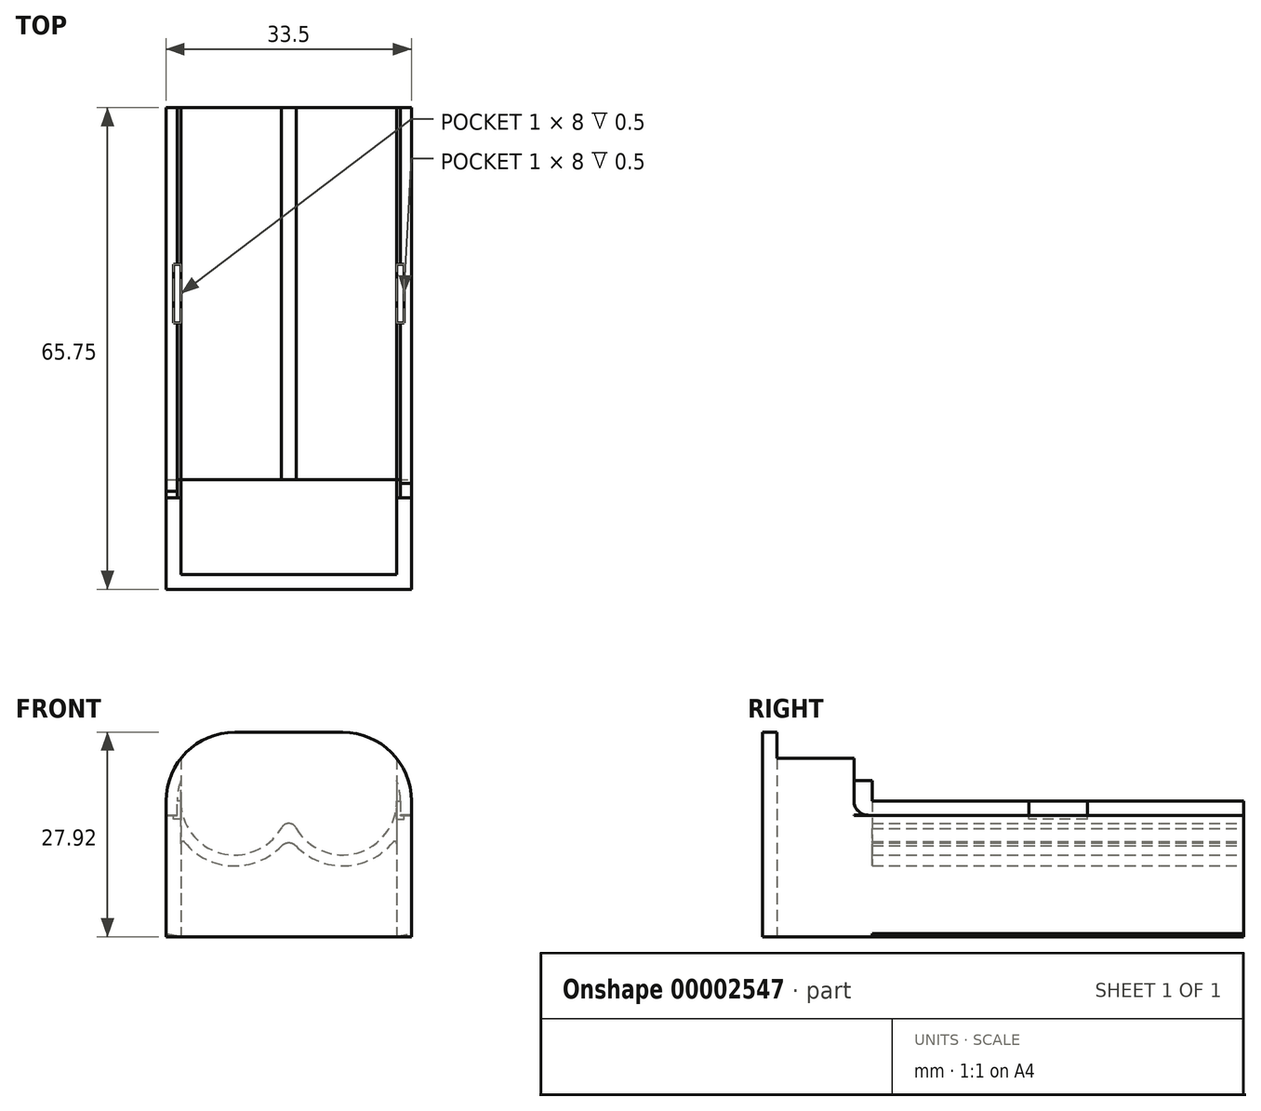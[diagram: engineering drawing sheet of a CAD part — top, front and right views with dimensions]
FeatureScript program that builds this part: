
annotation { "Feature Type Name" : "Feature", "Feature Type Description" : "" }
export const myFeature = defineFeature(function(context is Context, id is Id, definition is map)
    precondition{}
    {
        {
            var Q0;
            Q0=qCreatedBy(makeId("Front.planeOp"),FACE);
            var sketch = newSketch(context, id + "F0", { "sketchPlane" : qUnion([Q0])});
            skPoint(sketch, "E0.left.start.orphan", {"position": v(-29.5, 4.5) * mm});
            skArc(sketch, "E1", {"start": v(-29.31, 7.36) * mm, "mid": v(-23.14, 1.7) * mm, "end": v(-15.66, 5.45) * mm});
            skLineSegment(sketch, "E2.trimOffspring", {"start": v(-14.75, 9) * mm, "end": v(-14.75, 9) * mm});
            skPoint(sketch, "E3.end.orphan", {"position": v(-29.5, 9) * mm});
            skArc(sketch, "E4", {"start": v(-28.97, 3.35) * mm, "mid": v(-22.45, 0.13) * mm, "end": v(-15.71, 2.86) * mm});
            skPoint(sketch, "E5.top.start.orphan", {"position": v(-29.5, 0) * mm});
            skArc(sketch, "E6", {"start": v(-14.75, 3.25) * mm, "mid": v(-15.27, 3.15) * mm, "end": v(-15.71, 2.86) * mm});
            skLineSegment(sketch, "E7", {"start": v(-29.5, 9) * mm, "end": v(-30, 9) * mm});
            skLineSegment(sketch, "E8", {"start": v(-30, 9) * mm, "end": v(-30, 7.06) * mm});
            skLineSegment(sketch, "E9", {"start": v(-30.06, 7) * mm, "end": v(-31.5, 7) * mm});
            skLineSegment(sketch, "E10", {"start": v(-31.5, 7) * mm, "end": v(-31.5, -9.1) * mm});
            skLineSegment(sketch, "E11", {"start": v(-29.5, 3.16) * mm, "end": v(-29.5, -9.54) * mm});
            skArc(sketch, "E12", {"start": v(-28.97, 3.35) * mm, "mid": v(-29.3, 3.44) * mm, "end": v(-29.5, 3.16) * mm});
            skArc(sketch, "E13.trimOffspring", {"start": v(-14.75, 5.91) * mm, "mid": v(-15.37, 5.73) * mm, "end": v(-15.78, 5.24) * mm});
            skPoint(sketch, "E14.end.orphan", {"position": v(-0.19, 7.36) * mm});
            skPoint(sketch, "E14.start.orphan", {"position": v(0, 7.36) * mm});
            skPoint(sketch, "E15.center.orphan", {"position": v(-7.38, 9) * mm});
            skPoint(sketch, "E16.1.MirrorP", {"position": v(0, 0) * mm});
            skPoint(sketch, "E16.6.MirrorP", {"position": v(0, 4.5) * mm});
            skPoint(sketch, "E16.14.MirrorP", {"position": v(0, 9) * mm});
            skPoint(sketch, "E17.orphan", {"position": v(-29.31, 9) * mm});
            skArc(sketch, "E18", {"start": v(-29.5, 9) * mm, "mid": v(-29.45, 8.17) * mm, "end": v(-29.31, 7.36) * mm});
            skPoint(sketch, "E19.visualSharp", {"position": v(-30, 7) * mm});
            skArc(sketch, "E19.filletArc", {"start": v(-30.06, 7) * mm, "mid": v(-30.02, 7.02) * mm, "end": v(-30, 7.06) * mm});
            skLineSegment(sketch, "E20", {"start": v(-14.75, 5.91) * mm, "end": v(-14.75, 3.25) * mm});
            skArc(sketch, "E21.0.MirrorCS", {"start": v(0.56, 7) * mm, "mid": v(0.52, 7.02) * mm, "end": v(0.5, 7.06) * mm});
            skPoint(sketch, "E21.1.MirrorP", {"position": v(-0.19, 9) * mm});
            skLineSegment(sketch, "E21.2.MirrorCS", {"start": v(0, 9) * mm, "end": v(0.5, 9) * mm});
            skPoint(sketch, "E21.4.MirrorP", {"position": v(0.5, 7) * mm});
            skLineSegment(sketch, "E21.5.MirrorCS", {"start": v(0.56, 7) * mm, "end": v(2, 7) * mm});
            skLineSegment(sketch, "E21.7.MirrorCS", {"start": v(0.5, 9) * mm, "end": v(0.5, 7.06) * mm});
            skArc(sketch, "E21.9.MirrorCS", {"start": v(0, 9) * mm, "mid": v(-0.05, 8.17) * mm, "end": v(-0.19, 7.36) * mm});
            skArc(sketch, "E21.10.MirrorCS", {"start": v(-0.19, 7.36) * mm, "mid": v(-6.36, 1.7) * mm, "end": v(-13.84, 5.45) * mm});
            skArc(sketch, "E21.11.MirrorCS", {"start": v(-14.75, 3.25) * mm, "mid": v(-14.23, 3.15) * mm, "end": v(-13.79, 2.86) * mm});
            skArc(sketch, "E21.12.MirrorCS", {"start": v(-0.53, 3.35) * mm, "mid": v(-7.05, 0.13) * mm, "end": v(-13.79, 2.86) * mm});
            skLineSegment(sketch, "E21.13.MirrorCS", {"start": v(0, 3.16) * mm, "end": v(0, -9.54) * mm});
            skArc(sketch, "E21.15.MirrorCS", {"start": v(-14.75, 5.91) * mm, "mid": v(-14.13, 5.73) * mm, "end": v(-13.72, 5.24) * mm});
            skArc(sketch, "E21.16.MirrorCS", {"start": v(-0.53, 3.35) * mm, "mid": v(-0.2, 3.44) * mm, "end": v(0, 3.16) * mm});
            skLineSegment(sketch, "E21.19.MirrorCS", {"start": v(2, 7) * mm, "end": v(2, -9.1) * mm});
            skArc(sketch, "E22", {"start": v(-31.5, -9.1) * mm, "mid": v(-30.5, -9.33) * mm, "end": v(-29.5, -9.54) * mm});
            skArc(sketch, "E23.trimOffspring", {"start": v(0, -9.54) * mm, "mid": v(1, -9.33) * mm, "end": v(2, -9.1) * mm});
            skPoint(sketch, "E24.orphan", {"position": v(2, -6.36) * mm});
            skPoint(sketch, "E25.orphan", {"position": v(0, -6.36) * mm});
            skPoint(sketch, "E26.end.orphan", {"position": v(-29.5, -6.36) * mm});
            skPoint(sketch, "E27.orphan", {"position": v(-31.5, -6.36) * mm});
            skSolve(sketch);
        }
        {
            var Q0;
            Q0 = qSketchRegion(id + "F0", true);
            extrude(context, id + "F1", {"entities" : qUnion([Q0]), "depth" : 50.75 * mm});
        }
        {
            var Q0;
            Q0=makeQuery(id+"F1.opExtrude","SWEPT_FACE",FACE,{"disambiguationData":[OSD([sQuery(id+"F0.wireOp",EDGE,"E7")])]});
            var sketch = newSketch(context, id + "F2", { "sketchPlane" : qUnion([Q0])});
            skLineSegment(sketch, "E28.bottom", {"start": v(-29.5, -21.38) * mm, "end": v(-30.5, -21.38) * mm});
            skLineSegment(sketch, "E28.top", {"start": v(-29.5, -29.38) * mm, "end": v(-30.5, -29.38) * mm});
            skLineSegment(sketch, "E28.left", {"start": v(-29.5, -21.38) * mm, "end": v(-29.5, -29.38) * mm});
            skLineSegment(sketch, "E28.right", {"start": v(-30.5, -21.38) * mm, "end": v(-30.5, -29.38) * mm});
            skPoint(sketch, "E29", {"position": v(-29.5, -25.38) * mm});
            skSolve(sketch);
        }
        {
            var Q0;
            {var subQ7=sQuery(id+"F2.wireOp",EDGE,"E28.right");var subQ8=sQuery(id+"F2.wireOp",EDGE,"E28.left");Q0=qUnion([makeQuery(id+"F2.imprint","IMPRINT",FACE,{"disambiguationData":[TD([[makeQuery(id+"F2.imprint","IMPRINT",EDGE,{"derivedFrom":subQ7}),1.0]])]}),makeQuery(id+"F2.imprint","IMPRINT",FACE,{"disambiguationData":[TD([[makeQuery(id+"F2.imprint","IMPRINT",EDGE,{"derivedFrom":subQ8}),1.0]])]})]);}
            extrude(context, id + "F3", {"entities" : qUnion([Q0]), "operationType" : NewBodyOperationType.REMOVE, "oppositeDirection" : true, "depth" : 2.5 * mm});
        }
        {
            var Q0;
            Q0=makeQuery(id+"F1.opExtrude","SWEPT_FACE",FACE,{"disambiguationData":[OSD([sQuery(id+"F0.wireOp",EDGE,"E21.2.MirrorCS")])]});
            var sketch = newSketch(context, id + "F4", { "sketchPlane" : qUnion([Q0])});
            skLineSegment(sketch, "E30.bottom", {"start": v(0, -21.38) * mm, "end": v(1, -21.38) * mm});
            skLineSegment(sketch, "E30.top", {"start": v(0, -29.38) * mm, "end": v(1, -29.38) * mm});
            skLineSegment(sketch, "E30.left", {"start": v(0, -21.38) * mm, "end": v(0, -29.38) * mm});
            skLineSegment(sketch, "E30.right", {"start": v(1, -21.38) * mm, "end": v(1, -29.38) * mm});
            skPoint(sketch, "E31", {"position": v(0, -25.38) * mm});
            skSolve(sketch);
        }
        {
            var Q0;
            {var subQ7=sQuery(id+"F4.wireOp",EDGE,"E30.right");var subQ8=sQuery(id+"F4.wireOp",EDGE,"E30.left");Q0=qUnion([makeQuery(id+"F4.imprint","IMPRINT",FACE,{"disambiguationData":[TD([[makeQuery(id+"F4.imprint","IMPRINT",EDGE,{"derivedFrom":subQ7}),-1.0]])]}),makeQuery(id+"F4.imprint","IMPRINT",FACE,{"disambiguationData":[TD([[makeQuery(id+"F4.imprint","IMPRINT",EDGE,{"derivedFrom":subQ8}),-1.0]])]})]);}
            extrude(context, id + "F5", {"entities" : qUnion([Q0]), "operationType" : NewBodyOperationType.REMOVE, "oppositeDirection" : true, "depth" : 2.5 * mm});
        }
        {
            var Q0;
            Q0=makeQuery(id+"F1.opExtrude","CAP_FACE",FACE,{"disambiguationData":[OSD([sQuery(id+"F0.wireOp",EDGE,"E1"),sQuery(id+"F0.wireOp",EDGE,"E4"),sQuery(id+"F0.wireOp",EDGE,"E6"),sQuery(id+"F0.wireOp",EDGE,"E7"),sQuery(id+"F0.wireOp",EDGE,"E8"),sQuery(id+"F0.wireOp",EDGE,"E9"),sQuery(id+"F0.wireOp",EDGE,"E10"),sQuery(id+"F0.wireOp",EDGE,"E11"),sQuery(id+"F0.wireOp",EDGE,"E12"),sQuery(id+"F0.wireOp",EDGE,"E13.trimOffspring"),sQuery(id+"F0.wireOp",EDGE,"E19.filletArc"),sQuery(id+"F0.wireOp",EDGE,"E21.0.MirrorCS"),sQuery(id+"F0.wireOp",EDGE,"E21.2.MirrorCS"),sQuery(id+"F0.wireOp",EDGE,"E21.5.MirrorCS"),sQuery(id+"F0.wireOp",EDGE,"E21.7.MirrorCS"),sQuery(id+"F0.wireOp",EDGE,"E21.9.MirrorCS"),sQuery(id+"F0.wireOp",EDGE,"E21.11.MirrorCS"),sQuery(id+"F0.wireOp",EDGE,"E21.12.MirrorCS"),sQuery(id+"F0.wireOp",EDGE,"E21.13.MirrorCS"),sQuery(id+"F0.wireOp",EDGE,"E21.15.MirrorCS"),sQuery(id+"F0.wireOp",EDGE,"E21.16.MirrorCS"),sQuery(id+"F0.wireOp",EDGE,"E21.19.MirrorCS"),sQuery(id+"F0.wireOp",EDGE,"E22"),sQuery(id+"F0.wireOp",EDGE,"E23.trimOffspring")])],"isStart":false});
            var sketch = newSketch(context, id + "F6", { "sketchPlane" : qUnion([Q0])});
            skLineSegment(sketch, "E32.right", {"start": v(2, -9.54) * mm, "end": v(2, 9) * mm});
            skLineSegment(sketch, "E33", {"start": v(-31.5, 9) * mm, "end": v(-31.5, -9.54) * mm});
            skLineSegment(sketch, "E34", {"start": v(-31.5, -9.54) * mm, "end": v(2, -9.54) * mm});
            skArc(sketch, "E35", {"start": v(2, 9) * mm, "mid": v(-0.75, 15.63) * mm, "end": v(-7.37, 18.38) * mm});
            skArc(sketch, "E36", {"start": v(-22.13, 18.37) * mm, "mid": v(-28.75, 15.63) * mm, "end": v(-31.5, 9) * mm});
            skLineSegment(sketch, "E37", {"start": v(-7.38, 18.38) * mm, "end": v(-22.13, 18.38) * mm});
            skSolve(sketch);
        }
        {
            var Q0;
            {var subQ0=makeQuery(id+"F1.opExtrude","CAP_EDGE",EDGE,{"disambiguationData":[OSD([sQuery(id+"F0.wireOp",EDGE,"E23.trimOffspring")])],"isStart":false});var subQ1=makeQuery(id+"F6.imprint","IMPRINT",EDGE,{"derivedFrom":subQ0});var subQ20=makeQuery(id+"F6.imprint","IMPRINT",EDGE,{"derivedFrom":makeQuery(id+"F1.opExtrude","CAP_EDGE",EDGE,{"disambiguationData":[OSD([sQuery(id+"F0.wireOp",EDGE,"E1")])],"isStart":false})});var subQ21=sQuery(id+"F6.wireOp",EDGE,"E35");var subQ27=makeQuery(id+"F1.opExtrude","CAP_EDGE",EDGE,{"disambiguationData":[OSD([sQuery(id+"F0.wireOp",EDGE,"E22")])],"isStart":false});var subQ28=makeQuery(id+"F6.imprint","IMPRINT",EDGE,{"derivedFrom":subQ27});var subQ40=makeQuery(id+"F6.imprint","IMPRINT",EDGE,{"derivedFrom":makeQuery(id+"F1.opExtrude","CAP_EDGE",EDGE,{"disambiguationData":[OSD([sQuery(id+"F0.wireOp",EDGE,"E4")])],"isStart":false})});Q0=qUnion([makeQuery(id+"F6.imprint","IMPRINT",FACE,{"disambiguationData":[TD([[subQ1,-1.0]])]}),makeQuery(id+"F6.imprint","IMPRINT",FACE,{"disambiguationData":[TD([[makeQuery(id+"F6.imprint","IMPRINT",EDGE,{"derivedFrom":subQ21}),1.0]])]}),makeQuery(id+"F6.imprint","IMPRINT",FACE,{"disambiguationData":[TD([[subQ28,-1.0]])]}),makeQuery(id+"F6.imprint","IMPRINT",FACE,{"disambiguationData":[TD([[subQ40,-1.0]])]}),makeQuery(id+"F6.imprint","IMPRINT",FACE,{"disambiguationData":[TD([[subQ20,-1.0]])]})]);}
            extrude(context, id + "F7", {"entities" : qUnion([Q0]), "operationType" : NewBodyOperationType.ADD, "depth" : 15 * mm});
        }
        {
            var Q0;
            {var subQ2=sQuery(id+"F6.wireOp",EDGE,"E35");Q0=makeQuery(id+"F6.imprint","IMPRINT",FACE,{"disambiguationData":[TD([[makeQuery(id+"F6.imprint","IMPRINT",EDGE,{"derivedFrom":subQ2}),1.0]])]});}
            var sketch = newSketch(context, id + "F8", { "sketchPlane" : qUnion([Q0])});
            skArc(sketch, "E38", {"start": v(2, 9) * mm, "mid": v(-0.75, 15.63) * mm, "end": v(-7.37, 18.38) * mm});
            skArc(sketch, "E39", {"start": v(-22.13, 18.37) * mm, "mid": v(-28.75, 15.63) * mm, "end": v(-31.5, 9) * mm});
            skLineSegment(sketch, "E40", {"start": v(-7.38, 18.37) * mm, "end": v(-22.13, 18.37) * mm});
            skLineSegment(sketch, "E41", {"start": v(-31.5, 9) * mm, "end": v(-31.5, 7) * mm});
            skLineSegment(sketch, "E42", {"start": v(2, 7) * mm, "end": v(2, 9) * mm});
            skArc(sketch, "E43", {"start": v(0.5, 8.99) * mm, "mid": v(-1.8, 14.56) * mm, "end": v(-7.38, 16.87) * mm});
            skArc(sketch, "E44", {"start": v(-22.13, 16.88) * mm, "mid": v(-27.7, 14.57) * mm, "end": v(-30, 9) * mm});
            skLineSegment(sketch, "E45", {"start": v(-7.38, 16.88) * mm, "end": v(-22.13, 16.88) * mm});
            skLineSegment(sketch, "E46", {"start": v(2, 7) * mm, "end": v(0.5, 7) * mm});
            skLineSegment(sketch, "E47", {"start": v(0.5, 7) * mm, "end": v(0.5, 8.99) * mm});
            skLineSegment(sketch, "E48", {"start": v(-31.5, 7) * mm, "end": v(-30, 7) * mm});
            skLineSegment(sketch, "E49", {"start": v(-30, 7) * mm, "end": v(-30, 9) * mm});
            skSolve(sketch);
        }
        {
            var Q0;
            {var subQ2=sQuery(id+"F8.wireOp",EDGE,"E47");var subQ5=makeQuery(id+"F6.imprint","IMPRINT",EDGE,{"derivedFrom":makeQuery(id+"F1.opExtrude","CAP_EDGE",EDGE,{"disambiguationData":[OSD([sQuery(id+"F0.wireOp",EDGE,"E19.filletArc")])],"isStart":false})});var subQ6=makeQuery(id+"F8.imprint","IMPRINT",EDGE,{"derivedFrom":subQ5});Q0=qUnion([makeQuery(id+"F8.imprint","IMPRINT",FACE,{"disambiguationData":[TD([[makeQuery(id+"F8.imprint","IMPRINT",EDGE,{"derivedFrom":subQ2}),-1.0]])]}),makeQuery(id+"F8.imprint","IMPRINT",FACE,{"disambiguationData":[TD([[subQ6,-1.0]])]}),makeQuery(id+"F8.imprint","IMPRINT",FACE,{"disambiguationData":[TD([[makeQuery(id+"F8.imprint","IMPRINT",EDGE,{"derivedFrom":sQuery(id+"F8.wireOp",EDGE,"E38")}),1.0]])]})]);}
            extrude(context, id + "F9", {"entities" : qUnion([Q0]), "operationType" : NewBodyOperationType.REMOVE, "depth" : 2.5 * mm});
        }
        {
            var Q0;
            Q0=makeQuery(id+"F9.boolean.opBoolean","COPY",FACE,{"derivedFrom":makeQuery(id+"F9.opExtrude","SWEPT_FACE",FACE,{"disambiguationData":[OSD([sQuery(id+"F8.wireOp",EDGE,"E45")])]})});
            var sketch = newSketch(context, id + "F10", { "sketchPlane" : qUnion([Q0])});
            skLineSegment(sketch, "E50.bottom", {"start": v(-18.75, -50.75) * mm, "end": v(-10.75, -50.75) * mm});
            skLineSegment(sketch, "E50.top", {"start": v(-18.75, -53.25) * mm, "end": v(-10.75, -53.25) * mm});
            skLineSegment(sketch, "E50.left", {"start": v(-18.75, -50.75) * mm, "end": v(-18.75, -53.25) * mm});
            skLineSegment(sketch, "E50.right", {"start": v(-10.75, -50.75) * mm, "end": v(-10.75, -53.25) * mm});
            skPoint(sketch, "E51", {"position": v(-14.75, -50.75) * mm});
            skSolve(sketch);
        }
        {
            var Q0;
            Q0=makeQuery(id+"F10.imprint","IMPRINT",FACE,{"disambiguationData":[TD([[makeQuery(id+"F10.imprint","IMPRINT",EDGE,{"derivedFrom":sQuery(id+"F10.wireOp",EDGE,"E50.bottom")}),1.0]])]});
            extrude(context, id + "F11", {"entities" : qUnion([Q0]), "operationType" : NewBodyOperationType.REMOVE, "oppositeDirection" : true, "depth" : 2 * mm});
        }
        {
            var Q0;
            Q0=makeQuery(id+"F7.opExtrude","SWEPT_FACE",FACE,{"disambiguationData":[OSD([sQuery(id+"F6.wireOp",EDGE,"E34")])]});
            var sketch = newSketch(context, id + "F12", { "sketchPlane" : qUnion([Q0])});
            skLineSegment(sketch, "E52.bottom", {"start": v(0, 50.75) * mm, "end": v(-29.5, 50.75) * mm});
            skLineSegment(sketch, "E52.top", {"start": v(0, 63.75) * mm, "end": v(-29.5, 63.75) * mm});
            skLineSegment(sketch, "E52.left", {"start": v(0, 50.75) * mm, "end": v(0, 63.75) * mm});
            skLineSegment(sketch, "E52.right", {"start": v(-29.5, 50.75) * mm, "end": v(-29.5, 63.75) * mm});
            skSolve(sketch);
        }
        {
            var Q0;
            Q0=makeQuery(id+"F12.imprint","IMPRINT",FACE,{"disambiguationData":[TD([[makeQuery(id+"F12.imprint","IMPRINT",EDGE,{"derivedFrom":sQuery(id+"F12.wireOp",EDGE,"E52.top")}),1.0]])]});
            var Q1;
            Q1=makeQuery(id+"F7.opExtrude","SWEPT_FACE",FACE,{"disambiguationData":[OSD([sQuery(id+"F6.wireOp",EDGE,"E36")])]});
            extrude(context, id + "F13", {"entities" : qUnion([Q0]), "operationType" : NewBodyOperationType.REMOVE, "endBound" : BoundingType.UP_TO_NEXT, "oppositeDirection" : true, "endBoundEntity" : qUnion([Q1]), "depth" : 5 * mm});
        }
        {
            var Q0;
            {var subQ0=sQuery(id+"F0.wireOp",EDGE,"E21.7.MirrorCS");var subQ2=sQuery(id+"F0.wireOp",EDGE,"E21.0.MirrorCS");var subQ3=sQuery(id+"F8.wireOp",EDGE,"E43");Q0=makeQuery(id+"F9.boolean.opBoolean","MERGE",FACE,{"derivedFrom":[makeQuery(id+"F5.boolean.opBoolean","SPLIT",FACE,{"disambiguationData":[TD([makeQuery(id+"F5.opExtrude","SWEPT_FACE",FACE,{"disambiguationData":[OSD([sQuery(id+"F4.wireOp",EDGE,"E30.top")])]})])],"derivedFrom":makeQuery(id+"F1.opExtrude","SWEPT_FACE",FACE,{"disambiguationData":[OSD([subQ0])]})}),makeQuery(id+"F9.opExtrude","SWEPT_FACE",FACE,{"disambiguationData":[OSD([subQ3]),TDD([makeQuery(id+"F8.imprint","IMPRINT",EDGE,{"disambiguationData":[TD([[makeQuery(id+"F8.imprint","INTERSECT",VERTEX,{"derivedFrom":[makeQuery(id+"F6.imprint","IMPRINT",EDGE,{"derivedFrom":makeQuery(id+"F1.opExtrude","CAP_EDGE",EDGE,{"disambiguationData":[OSD([subQ2])],"isStart":false})}),subQ3,sQuery(id+"F8.wireOp",EDGE,"E47")]}),1.0]])],"derivedFrom":subQ3})])]})]});}
            var sketch = newSketch(context, id + "F14", { "sketchPlane" : qUnion([Q0])});
            skLineSegment(sketch, "E53.top", {"start": v(-53.25, 7.06) * mm, "end": v(-51.3, 7.06) * mm});
            skLineSegment(sketch, "E53.left", {"start": v(-53.25, 9) * mm, "end": v(-53.25, 7.06) * mm});
            skArc(sketch, "E54", {"start": v(-53.25, 9) * mm, "mid": v(-52.68, 7.63) * mm, "end": v(-51.3, 7.06) * mm});
            skSolve(sketch);
        }
        {
            var Q0;
            Q0=makeQuery(id+"F14.imprint","IMPRINT",FACE,{"disambiguationData":[TD([[makeQuery(id+"F14.imprint","IMPRINT",EDGE,{"derivedFrom":sQuery(id+"F14.wireOp",EDGE,"E53.top")}),1.0]])]});
            extrude(context, id + "F15", {"entities" : qUnion([Q0]), "operationType" : NewBodyOperationType.ADD, "depth" : 1.5 * mm});
        }
        {
            var Q0;
            {var subQ0=sQuery(id+"F0.wireOp",EDGE,"E8");Q0=makeQuery(id+"F9.boolean.opBoolean","MERGE",FACE,{"derivedFrom":[makeQuery(id+"F3.boolean.opBoolean","SPLIT",FACE,{"disambiguationData":[TD([makeQuery(id+"F3.opExtrude","SWEPT_FACE",FACE,{"disambiguationData":[OSD([sQuery(id+"F2.wireOp",EDGE,"E28.top")])]})])],"derivedFrom":makeQuery(id+"F1.opExtrude","SWEPT_FACE",FACE,{"disambiguationData":[OSD([subQ0])]})}),makeQuery(id+"F9.opExtrude","SWEPT_FACE",FACE,{"disambiguationData":[OSD([sQuery(id+"F8.wireOp",EDGE,"E49")])]})]});}
            var sketch = newSketch(context, id + "F16", { "sketchPlane" : qUnion([Q0])});
            skLineSegment(sketch, "E55", {"start": v(53.25, 7) * mm, "end": v(53.25, 9) * mm});
            skLineSegment(sketch, "E56", {"start": v(53.25, 7) * mm, "end": v(51.35, 6.38) * mm});
            skArc(sketch, "E57", {"start": v(51.35, 6.38) * mm, "mid": v(52.72, 7.38) * mm, "end": v(53.25, 9) * mm});
            skSolve(sketch);
        }
        {
            var Q0;
            {var subQ4=sQuery(id+"F16.wireOp",EDGE,"E55");var subQ5=sQuery(id+"F16.wireOp",EDGE,"E56");Q0=qUnion([makeQuery(id+"F16.imprint","IMPRINT",FACE,{"disambiguationData":[TD([[makeQuery(id+"F16.imprint","IMPRINT",EDGE,{"derivedFrom":subQ5}),-1.0]])]}),makeQuery(id+"F16.imprint","IMPRINT",FACE,{"disambiguationData":[TD([[makeQuery(id+"F16.imprint","IMPRINT",EDGE,{"derivedFrom":subQ4}),1.0]])]})]);}
            extrude(context, id + "F17", {"entities" : qUnion([Q0]), "operationType" : NewBodyOperationType.ADD, "depth" : 1.5 * mm});
        }
    });
